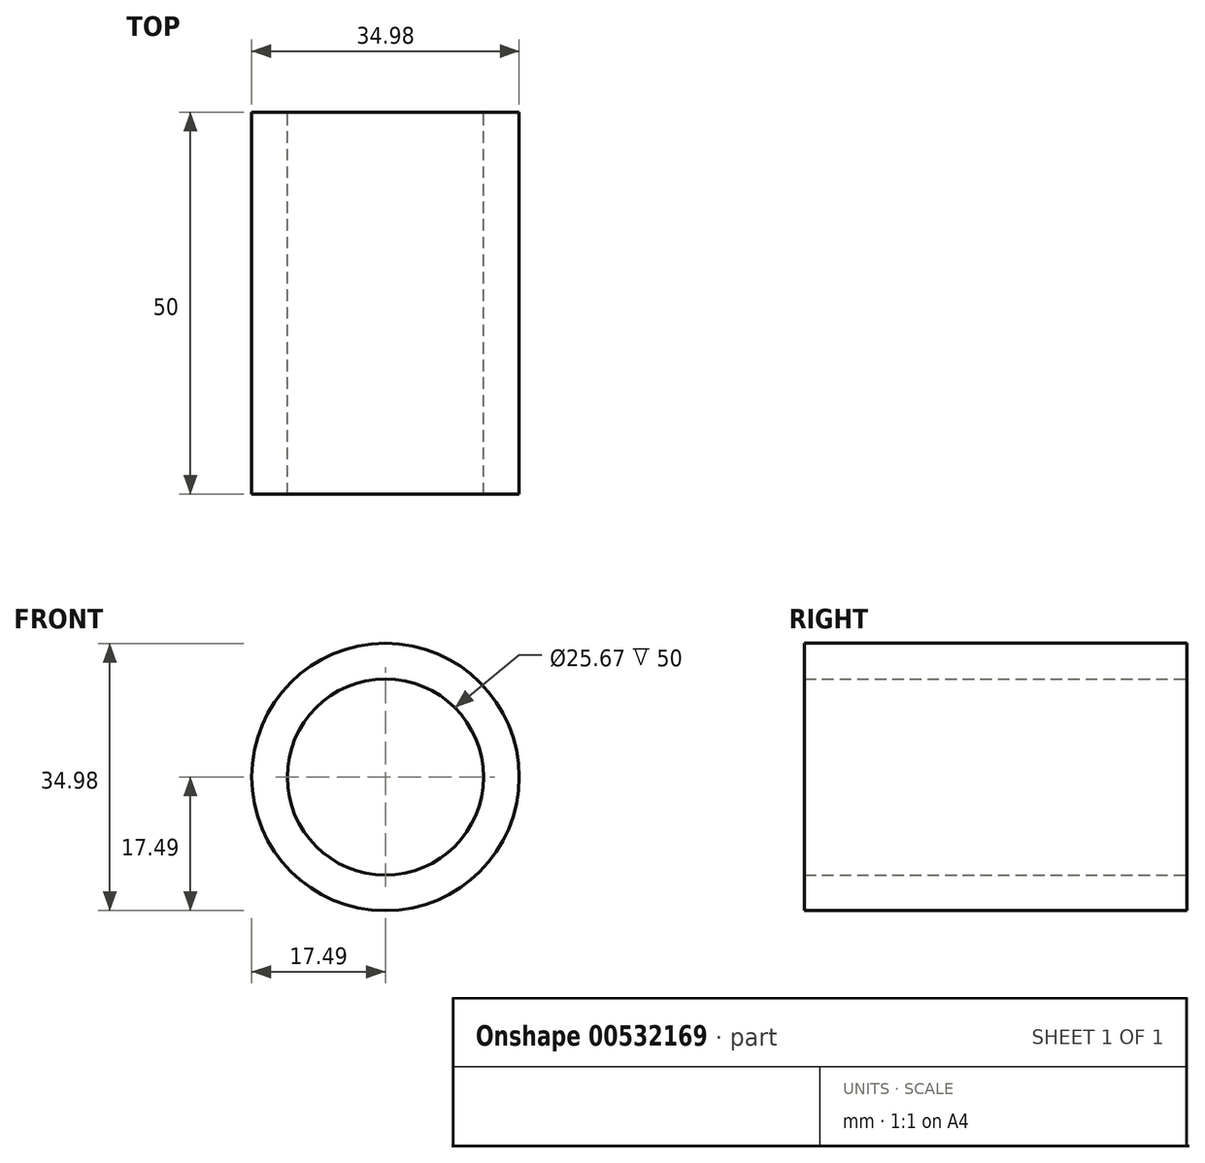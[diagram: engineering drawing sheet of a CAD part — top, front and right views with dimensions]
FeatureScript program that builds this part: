
annotation { "Feature Type Name" : "Feature", "Feature Type Description" : "" }
export const myFeature = defineFeature(function(context is Context, id is Id, definition is map)
    precondition{}
    {
        {
            var Q0;
            Q0=qCreatedBy(makeId("Front.planeOp"),FACE);
            var sketch = newSketch(context, id + "F0", { "sketchPlane" : qUnion([Q0])});
            skCircle(sketch, "E0", {"center": v(0, 0) * mm, "radius": 17.5 * mm});
            skCircle(sketch, "E1", {"center": v(0, 0) * mm, "radius": 12.83 * mm});
            skSolve(sketch);
        }
        {
            var Q0;
            Q0=makeQuery(id+"F0.imprint","IMPRINT",FACE,{"disambiguationData":[TD([[makeQuery(id+"F0.imprint","IMPRINT",EDGE,{"derivedFrom":sQuery(id+"F0.wireOp",EDGE,"E0")}),1.0]])]});
            extrude(context, id + "F1", {"entities" : qUnion([Q0]), "depth" : 50 * mm, "offsetDistance" : 25 * mm});
        }
    });
